# Revit family: WashbasinUnit-100cm-Vitra-PluralSeries-64044+64045+64046+64047+64048
name_source: partatom
category: Furniture Systems
revit_build: Autodesk Revit 2017 (Build: 20160225_1515(x64)
units: mm (PartAtom-declared; Revit-internal decimal feet)

## family parameters
Cut with Voids When Loaded = No
Host = Face
OmniClass Number = 23.40.00.00
OmniClass Title = Equipment and Furnishings
Part Type = Normal
Room Calculation Point = No
Round Connector Dimension = Use Diameter
Shared = Yes

## types (5) — shared parameters
BIMobject category = Bathroom compound units
Construction Type = Face Mounted
Depth = 520 mm  [stored 1.70604 ft]
Description = Plural Washbasin Unit
Design country = Turkey
Height = 800 mm
IFC Classification = Furniture
Manufacturer = Vitra
Manufacturer name = Vitra
Masterformat 2014 Code = 13 42 13
Masterformat 2014 Description = Bathroom Unit Modules
NBS Referans Code = 35-75-08
NBS Referans Description = Bathroom Cabinets
Nominal height = 0.000
Nominal width = 0.000
OmniClass Code = 23-31 25 13
OmniClass Description = Bathroom Cabinets
Primary Material = Vitra-DarkOlive
Product certification = https://vitraglobal.com
Product data url = https://www.vitraglobal.com
Product family = Plural
Product group = Washbasin Unit
Secondary Material = Vitra-AmericanValnut
Technical description = https://www.vitraglobal.com
Thrid Material = Vitra-AmericanValnut
UNSPSC Code = 301815
UNSPSC Description = Bathroom Cabinets
URL = https://vitraglobal.com
Uniclass 1.4 Code = L8241
Uniclass 1.4 Description = Bathroom Cabinets
Uniclass 2.0 Code = PR-35-75-08
Uniclass 2.0 Description = Bathroom Cabinets
Uniclass 2015 Code = Pr_40_20_93
Uniclass 2015 Name = Wash basins, sinks and troughs
Uniformat II Code = E20
Uniformat II Description = FURNISHINGS
Warranty Period (Year) = 2
Weight Net (kg) = 45,300
Width = 885 mm
Youtube = https://www.youtube.com
zero-valued in all types: Default Elevation

## per-type parameters (varying)
| type | Article No. (default) | Model | Product SKU | Visibil |
| WashbasinUnit-100cm-Vitra-Plural_64044 | 64044 | 64044 | 64044 | WashBasin-100cm-Vitra_PluralSeries_7813-001-0041 : Vitra_Plural_WashBasin-100cm_7813-001-0041 |
| WashbasinUnit-100cm-Vitra-Plural_64045 | 64045 | 64045 | 64045 | WashBasin-100cm-Vitra_PluralSeries_7813-001-0041 : Vitra_Plural_WashBasin-100cm_7813-003-0041 |
| WashbasinUnit-100cm-Vitra-Plural_64046 | 64046 | 64046 | 64046 | WashBasin-100cm-Vitra_PluralSeries_7813-001-0041 : Vitra_Plural_WashBasin-100cm_7813-020-0041 |
| WashbasinUnit-100cm-Vitra-Plural_64047 | 64047 | 64047 | 64047 | WashBasin-100cm-Vitra_PluralSeries_7813-001-0041 : Vitra_Plural_WashBasin-100cm_7813-050-0041 |
| WashbasinUnit-100cm-Vitra-Plural_64048 | 64048 | 64048 | 64048 | WashBasin-100cm-Vitra_PluralSeries_7813-001-0041 : Vitra_Plural_WashBasin-100cm_7813-083-0041 |

note: [stored X ft] marks values corroborated as IEEE doubles in the binary element streams (Revit-internal decimal feet)

## geometry (parser evidence)
native form markers: Sweep x5
no freeform markers — native parametric forms only
